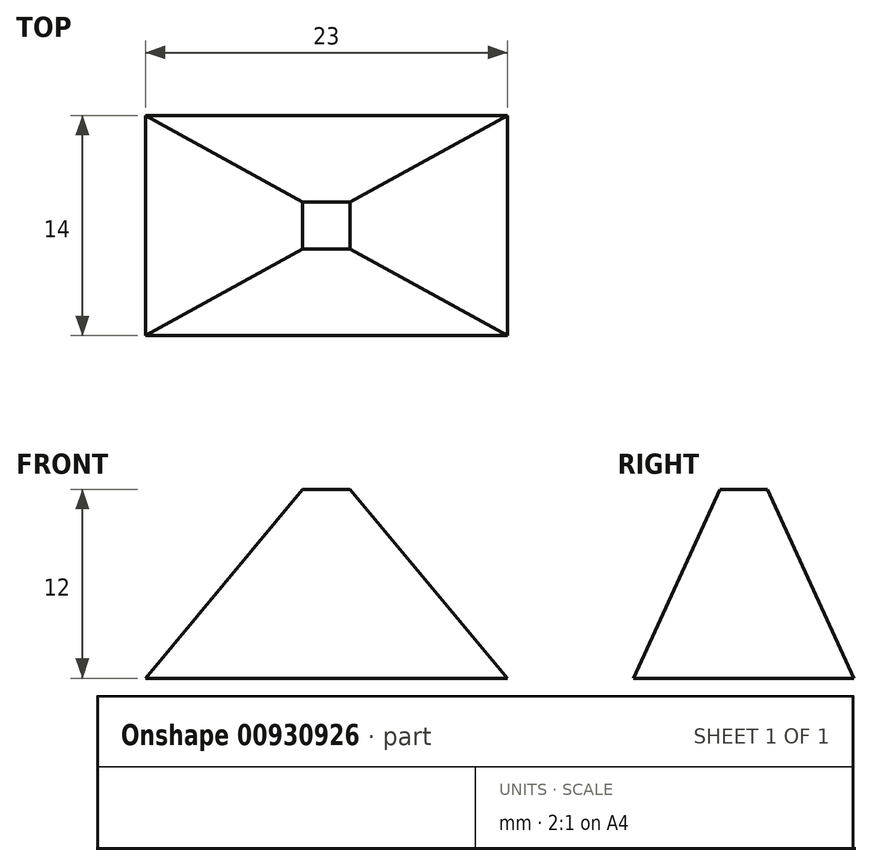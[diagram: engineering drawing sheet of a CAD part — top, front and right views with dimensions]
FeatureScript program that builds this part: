
annotation { "Feature Type Name" : "Feature", "Feature Type Description" : "" }
export const myFeature = defineFeature(function(context is Context, id is Id, definition is map)
    precondition{}
    {
        {
            var Q0;
            Q0=qCreatedBy(makeId("Top.planeOp"),FACE);
            var sketch = newSketch(context, id + "F0", { "sketchPlane" : qUnion([Q0])});
            skLineSegment(sketch, "E0.bottom", {"start": v(11.5, 7) * mm, "end": v(-11.5, 7) * mm});
            skLineSegment(sketch, "E0.top", {"start": v(11.5, -7) * mm, "end": v(-11.5, -7) * mm});
            skLineSegment(sketch, "E0.left", {"start": v(11.5, 7) * mm, "end": v(11.5, -7) * mm});
            skLineSegment(sketch, "E0.right", {"start": v(-11.5, 7) * mm, "end": v(-11.5, -7) * mm});
            skPoint(sketch, "E0.middle", {"position": v(0, 0) * mm});
            skSolve(sketch);
        }
        {
            var Q0;
            Q0 = qSketchRegion(id + "F0", true);
            extrude(context, id + "F1", {"entities" : qUnion([Q0]), "depth" : 12 * mm, "offsetDistance" : 25 * mm});
        }
        {
            var Q0;
            Q0=makeQuery(id+"F1.opExtrude","CAP_EDGE",EDGE,{"disambiguationData":[OSD([sQuery(id+"F0.wireOp",EDGE,"E0.right")])],"isStart":false});
            var Q1;
            Q1=makeQuery(id+"F1.opExtrude","CAP_EDGE",EDGE,{"disambiguationData":[OSD([sQuery(id+"F0.wireOp",EDGE,"E0.left")])],"isStart":false});
            chamfer(context, id + "F2", {"entities" : qUnion([Q0, Q1]), "chamferType" : ChamferType.TWO_OFFSETS, "width1" : 10 * mm, "oppositeDirection" : false, "width2" : 12 * mm, "tangentPropagation" : true});
        }
        {
            var Q0;
            Q0=makeQuery(id+"F1.opExtrude","CAP_EDGE",EDGE,{"disambiguationData":[OSD([sQuery(id+"F0.wireOp",EDGE,"E0.top")])],"isStart":false});
            var Q1;
            Q1=makeQuery(id+"F1.opExtrude","CAP_EDGE",EDGE,{"disambiguationData":[OSD([sQuery(id+"F0.wireOp",EDGE,"E0.bottom")])],"isStart":false});
            chamfer(context, id + "F3", {"entities" : qUnion([Q0, Q1]), "chamferType" : ChamferType.TWO_OFFSETS, "width1" : 12 * mm, "oppositeDirection" : false, "width2" : 5.5 * mm, "tangentPropagation" : true});
        }
    });
